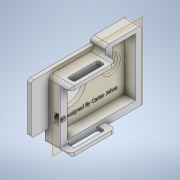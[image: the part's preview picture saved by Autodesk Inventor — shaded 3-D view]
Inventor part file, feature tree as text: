
AUTODESK INVENTOR PART (.ipt)
format: ipt  version: 2020.4 (Build 244396000, 396)  size: 1,208,320 bytes
history: native  units: in
note: dims shown in document units (in); Inventor stores cm internally (conversion verified against a paired STEP export)
features: sketch x28, extrude x20, fillet x11, projected_geometry x10, plane x3, loft x2, emboss x1
ambient origin geometry x8: Origin, YZ Plane, XZ Plane, XY Plane, X Axis, Y Axis, Z Axis, Center Point
bodies: Solid1 (feature_tree)
feature tree (75):
  extrude  "Extrusion1"  Depth=1.67in
  extrude  "Extrusion2"  Depth=0.25in
  sketch  "Sketch3"  dims[d4=0.4in d5=0.0in d6=1.2in]
  plane  "Work Plane1"
  sketch  "Sketch4"  dims[d7=0.5in d8=0.5in]
  sketch  "Sketch5"  dims[d9=0.28in d10=0.0in d11=1.25in d12=2.0in]
  sketch  "Sketch6"  dims[d13=2.0in d14=1.5in]
  sketch  "Sketch7"  dims[d15=1.5in d16=0.25in]
  loft  "Loft1"
  loft  "Loft2"
  extrude  "Extrusion3"  Depth=1.25in
  fillet  "Fillet1"  Radius=2.0in
  extrude  "Extrusion4"  Depth=1.5in
  sketch  "Sketch10"  dims[d24=0.0in d25=90.0deg d26=1.0in d27=0.0in]
  extrude  "Extrusion5"  Depth=0.25in
  extrude  "Extrusion6"  TaperAngle=0.0deg  [1 undecoded]
  extrude  "Extrusion7"  TaperAngle=0.0deg  [1 undecoded]
  extrude  "Extrusion8"  Depth=1.0in TaperAngle=0.0deg
  extrude  "Extrusion9"  Depth=0.25in TaperAngle=0.0deg
  fillet  "Fillet2"  [1 undecoded]
  fillet  "Fillet3"  Radius=0.25in
  sketch  "Sketch16"  dims[d50=0.15in d51=1.0in d52=0.0in d53=0.05in]
  extrude  "Extrusion10"  Depth=0.15in
  fillet  "Fillet4"  Radius=1.0in
  emboss  "Emboss1"
  extrude  "Extrusion11"  Depth=0.15in TaperAngle=0.0deg
  fillet  "Fillet5"  Radius=0.15in
  fillet  "Fillet6"  Radius=1.0in
  fillet  "Fillet7"  Radius=1.0in
  extrude  "Extrusion12"  Depth=0.05in
  extrude  "Extrusion13"  Depth=0.3in
  extrude  "Extrusion14"  Depth=0.05in TaperAngle=0.0deg
  fillet  "Fillet8"  Radius=0.05in
  extrude  "Extrusion15"  Depth=0.5in
  extrude  "Extrusion16"  Depth=0.6in
  fillet  "Fillet9"  Radius=0.1in
  fillet  "Fillet10"  Radius=0.05in
  plane  "Work Plane2"
  extrude  "Extrusion17"  Depth=0.1in
  extrude  "Extrusion18"  Depth=1.0in TaperAngle=0.0deg
  extrude  "Extrusion19"  Depth=0.125in
  plane  "Work Plane3"
  extrude  "Extrusion20"  Depth=0.125in
  fillet  "Fillet11"  Radius=0.25in
  sketch  "Sketch1"  dims[d0=2.42in d1=1.67in]
  sketch  "Sketch2"  dims[d2=0.25in d3=0.8in]
  sketch  "Sketch8"  dims[d17=0.2497in d18=0.0in d19=90.0deg]
  sketch  "Sketch9"  dims[d20=0.0in d21=90.0deg d22=0.0in d23=90.0deg]
  sketch  "Sketch11"  dims[d28=0.125in d29=1.0in d30=0.0in d31=0.0in d32=0.25in]
  sketch  "Sketch12"  dims[d33=0.15in d34=0.15in d35=1.0in d36=0.0in]
  projected_geometry  "Projected Loop1"
  projected_geometry  "Projected Loop2"
  projected_geometry  "Projected Loop3"
  sketch  "Sketch13"  dims[d37=1.0in d38=0.0in d39=1.0in d40=0.0in d41=0.15in d42=1.0in d43=0.0in d44=1.0in d45=0.0in]
  projected_geometry  "Projected Loop4"
  sketch  "Sketch14"  dims[d46=0.125in d47=0.05in]
  projected_geometry  "Projected Loop5"
  sketch  "Sketch15"  dims[d48=0.0in d49=0.3in]
  projected_geometry  "Projected Loop6"
  projected_geometry  "Projected Loop7"
  sketch  "Sketch17"  dims[d54=0.1in d55=0.0in d56=0.5in]
  sketch  "Sketch18"  dims[d57=0.5in d58=0.6in d59=0.1in d60=0.0in d61=0.05in]
  sketch  "Sketch19"  dims[d62=0.1in d63=0.1in]
  sketch  "Sketch20"  dims[d64=1.0in d65=0.0in d66=1.0in d67=0.0in]
  projected_geometry  "Projected Loop8"
  sketch  "Sketch21"  dims[d68=1.0in d69=0.0in d70=0.125in]
  sketch  "Sketch22"  dims[d71=0.25in d72=0.125in d73=0.25in]
  sketch  "Sketch23"  dims[d74=0.125in d75=0.0in]
  projected_geometry  "Projected Loop9"
  sketch  "Sketch24"  dims[d76=0.25in]
  projected_geometry  "Projected Loop10"
  sketch  "Sketch25"  dims[d77=0.15in]
  sketch  "Sketch26"  dims[d78=0.125in d79=0.0in]
  sketch  "Sketch27"  dims[d80=0.125in]
  sketch  "Sketch28"  dims[d81=0.0625in d82=-0.14in d83=0.915in d84=0.0in d85=0.2in d86=0.731in d87=0.375in d88=0.0in d89=0.053in d90=0.12in d91=0.12in d92=0.12in d93=0.125in d94=0.0in d95=-0.125in d96=0.32in d97=0.32in d98=0.16in d100=0.16in d101=0.15in d102=0.0in d104=0.425in d105=0.025in]
note: 3 required parameter values undecoded (feature->parameter linkage not recoverable at this tier; creation-order binding heuristic only, values carry confidence <= 0.55)
